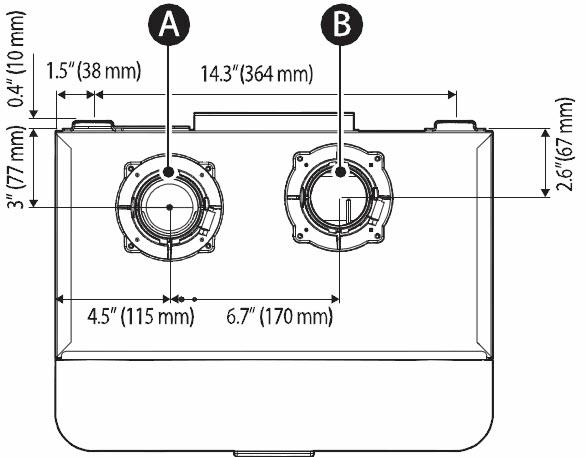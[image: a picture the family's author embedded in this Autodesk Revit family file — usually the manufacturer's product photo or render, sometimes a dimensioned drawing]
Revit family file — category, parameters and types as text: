
# Revit family: Water_Heater-Racks-Navien-NPE-15_Unit_Front-Wall-02
name_source: partatom
category: Mechanical Equipment
revit_build: Autodesk Revit 2016 (Build: 20150220_1215(x64)
units: mm (PartAtom-declared; Revit-internal decimal feet)

## family parameters
Cut with Voids When Loaded = No
Host = Face
OmniClass Number = 23.65.35.11
OmniClass Title = Supply Water Heaters
Part Type = Normal
Room Calculation Point = No
Round Connector Dimension = Use Diameter
Shared = No

## types (4) — shared parameters
2" Exhaust/Intake = Yes
3" Exhaust/Intake = No
Apparent Load = 0 VA
Assembly Code = D3010500
Certifications = Energy Star | AHRI | CSA | CSA | NFS
Cold Water Inlet = 1"
Configuration = NPE_F15_4F4F-4F3F
Default Elevation = 48 "
Depth = 23.8 "
Description = 15 Unit Front
Exhaust = 2"
Finish = Metal - Navien - White
Flow Rate = 1 GPM
Flow Rate Note = 35°F (19°C) temp rise: 11.2 GPM (42 L/m) | 45°F (25°C) temp rise: 8.7 GPM (33 L/m) | 67°F (36°C) temp rise: NPE-240A: 5.6 GPM(21 L/m), NPE-240S: 5.7 GPM(22 L/m)
Frequency = 60 Hz
Gas Inlet = 1"
Heating Capacity = 120000.0 Btu/h
Heating Capacity Note = 19,900–199,900 (BTU/H)
Height = 65.5 "
Hot Water Outlet = 1"
Ignition = Electronic ignition
Installation Type = Indoor
Intake = 2"
Keynote = 22 33 00.A1
Manifold(s) = (1) 30019041A + (3) 30019043A
Manufacturer = Navien, Inc.
Manufacturer Fax Number = (949) 420-0430
Natural Gas Manifold Pressure = -0.05" WC to -0.58" WC
Natural Gas Supply Pressure = 3.5"–10.5" WC
Number of Poles = 1
Phase = 1
Power Factor = 1
Product Documentation Link = https://www.navieninc.com
Product Name = NPE Series Tankless Water Heaters w/ Racks
Product Page URL = https://www.navieninc.com
Propane Gas Manifold Pressure = -0.10" WC to -0.78" WC
Propane Gas Supply Pressure = 8"–13" WC
Required Cascade Operation Accessory = (15) 30014367A (Common Vent Damper & Cascade Communication Cable) or (14) GXXX000546 (Individual Vent Cascade Communication Cable)
Type Comments = For Wall Mount RL Manifold systems- Exclude Base & Add-on Racks
URL = https://www.navieninc.com
Venting = Exhaust: 2" PVC, CPVC, PP, SS / 2" special gas vent type BH (Class II, A/B/C) | Intake: 2" PVC, CPVC, PP, SS / 2" special gas vent type BH (Class II, A/B/C) | Vent clearances: 0" to combustibles
Venting Type = Forced draft direct vent
Version = 2016 - v1.0.a
Voltage = 120 V
Water Pressure = 15–150 PSI
Wi-Fi Ready = NaviLink Wi-Fi Control: PBCM-AS-001
Width = 322.3 "

## per-type parameters (varying)
| type | Constraints | Model | Natural Gas | Propane Gas | Recirculation Inlet | Recirculation Inlet Visibility | Tankless Water Heaters | Weight |
| Natural Gas - Recirculating System - NPE-240A(Advanced)-NG | 6 | (15) NPE-240A-NG | Yes | No | 0" | Yes | (15) NPE-240A-NG | 82.00 lbf |
| Natural Gas - NPE-240S(Standard)-NG | 7 | (15) NPE-240S-NG | Yes | No | 1" | No | (15) NPE-240S-NG | 75.00 lbf |
| Propane Gas - Recirculating System - NPE-240A(Advanced)-LPG | 6 | (15) NPE-240A-LPG | No | Yes | 0" | Yes | (15) NPE-240A-LPG | 82.00 lbf |
| Propane Gas - NPE-240S(Standard)-LPG | 7 | (15) NPE-240S-LPG | No | Yes | 1" | No | (15) NPE-240S-LPG | 75.00 lbf |

## geometry (parser evidence)
native form markers: Sweep x10
no freeform markers — native parametric forms only
